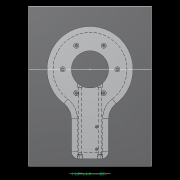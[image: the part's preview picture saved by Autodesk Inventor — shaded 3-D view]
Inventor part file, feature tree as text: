
AUTODESK INVENTOR PART (.ipt)
format: ipt  version: 2022.2 (Build 262287010, 287A)  size: 793,600 bytes
history: native  units: mm
features: extrude x36, sketch x23, other x20, pattern_circular x11, plane x7, fillet x6, draft x3, move_body x2, revolve x2, chamfer x2, projected_geometry x1
ambient origin geometry x8: Origin, YZ Plane, XZ Plane, XY Plane, X Axis, Y Axis, Z Axis, Center Point
bodies: Solid5 (feature_tree)
feature tree (113):
  other  "CrossSection1"
  other  "CrossSection2"
  sketch  "Sketch7"  dims[d167=8.972256mm]
  other  "Roller1"
  other  "Roller2"
  sketch  "Sketch22"  dims[d173=10.814812mm]
  sketch  "Sketch2"  dims[d57=4.025mm d90=61.984365mm]
  sketch  "Sketch23"  dims[d201=75.0mm d232=0.0mm d233=3600.0mm]
  other  "RevRoller1"
  fillet  "Fillet1"  Radius=59.246882mm
  extrude  "Extrusion39"  Depth=61.984365mm
  pattern_circular  "Circular Pattern13"  Count=360  [1 undecoded]
  move_body  "Move Body7"
  revolve  "Revolution13"  [1 undecoded]
  fillet  "Fillet3"  Radius=0.025mm
  pattern_circular  "Circular Pattern14"  Count=24  [1 undecoded]
  move_body  "Move Body6"
  revolve  "Revolution14"  [1 undecoded]
  other  "OuterRim_Top2"
  other  "OuterRim_Bottom2"
  plane  "Work Plane8"
  sketch  "Sketch49"  dims[d352=0.025mm]
  sketch  "Sketch50"  dims[d354=0.025mm]
  sketch  "Sketch51"  dims[d355=16.1595mm]
  extrude  "Extrusion40"  Depth=0.025mm
  extrude  "Extrusion41"  Depth=1.308997mm
  extrude  "Extrusion42"  Depth=0.5mm
  extrude  "Extrusion43"  TaperAngle=360.0deg  [1 undecoded]
  sketch  "Sketch52"  dims[d356=16.159664mm]
  extrude  "Extrusion44"  Depth=7.0mm
  extrude  "Extrusion45"  Depth=7.0mm
  extrude  "Extrusion46"  Depth=7.0mm
  extrude  "Extrusion47"  Depth=7.0mm
  pattern_circular  "Circular Pattern32"  [2 undecoded]
  pattern_circular  "Circular Pattern33"  [2 undecoded]
  sketch  "Sketch57"  dims[d358=360.0deg]
  extrude  "Extrusion50"  TaperAngle=0.0deg  [1 undecoded]
  extrude  "Extrusion51"  TaperAngle=0.0deg  [1 undecoded]
  pattern_circular  "Circular Pattern34"  [2 undecoded]
  extrude  "Extrusion52"  Depth=7.0mm
  extrude  "Extrusion53"  Depth=7.0mm
  pattern_circular  "Circular Pattern35"  [2 undecoded]
  plane  "Work Plane9"
  sketch  "Sketch59"  dims[d361=360.0deg d363=1.308997mm]
  extrude  "Extrusion54"  Depth=7.0mm
  draft  "FaceDraft7"
  extrude  "Extrusion59"  Depth=7.0mm
  extrude  "Extrusion60"  TaperAngle=90.0deg  [1 undecoded]
  fillet  "Fillet5"  [1 undecoded]
  plane  "Work Plane10"
  extrude  "Extrusion63"  TaperAngle=90.0deg  [1 undecoded]
  fillet  "Fillet7"  Radius=75.0mm
  plane  "Work Plane11"
  sketch  "Sketch61"  dims[d371=1.0mm d372=1.308997mm]
  sketch  "Sketch62"  dims[d373=90.0deg d374=0.5mm]
  extrude  "Extrusion64"  Depth=7.0mm
  extrude  "Extrusion65"  TaperAngle=0.0deg  [1 undecoded]
  fillet  "Fillet8"  Radius=0.436332mm
  extrude  "Extrusion66"  Depth=2.0mm TaperAngle=0.0deg
  fillet  "Fillet9"  Radius=2.5mm
  extrude  "Extrusion67"  Depth=8.0mm
  plane  "Work Plane7"
  sketch  "Sketch47"  dims[d350=47.575427mm]
  extrude  "Rotor_Ring"  Depth=8.0mm
  draft  "FaceDraft2"
  sketch  "Sketch30"  dims[d343=16.1595mm d344=16.159664mm d345=0.025mm]
  plane  "Work Plane5"
  other  "Rotor Featurs"
  other  "RotorRim_Bottom"
  extrude  "Extrusion24"  Depth=7.0mm TaperAngle=30.0deg
  extrude  "Extrusion25"  Depth=7.0mm
  extrude  "Extrusion26"  Depth=7.0mm TaperAngle=30.0deg
  pattern_circular  "Circular Pattern23"  [2 undecoded]
  sketch  "Sketch41"  dims[d347=0.1mm]
  extrude  "Extrusion27"  Depth=7.0mm
  extrude  "Extrusion28"  Depth=7.0mm
  pattern_circular  "Circular Pattern24"  Count=10  [1 undecoded]
  extrude  "Extrusion29"  Depth=2.0mm
  extrude  "Extrusion30"  Depth=7.0mm
  extrude  "Extrusion31"  Depth=7.0mm
  pattern_circular  "Circular Pattern25"  [2 undecoded]
  sketch  "Sketch42"  dims[d348=0.1mm]
  extrude  "Extrusion32"  Depth=7.0mm
  extrude  "Extrusion33"  Depth=7.0mm
  extrude  "Extrusion34"  Depth=7.0mm
  extrude  "Extrusion35"  Depth=7.0mm
  pattern_circular  "Circular Pattern26"  [2 undecoded]
  pattern_circular  "Circular Pattern27"  [2 undecoded]
  chamfer  "Chamfer1"  Distance=3.0mm
  chamfer  "Chamfer2"  Distance=2.4mm
  draft  "FaceDraft4"
  plane  "Work Plane6"
  sketch  "Sketch43"  dims[d349=47.575591mm]
  extrude  "Extrusion37"  TaperAngle=0.0deg  [1 undecoded]
  extrude  "Extrusion38"  TaperAngle=0.0deg  [1 undecoded]
  other  "2D Equation Curve1"
  sketch  "Sketch40"  dims[d346=0.025mm]
  other  "Work Axis6"
  other  "Work Axis7"
  other  "Work Axis8"
  other  "Work Axis9"
  other  "Work Axis10"
  other  "Work Point1"
  other  "Work Point2"
  other  "Work Point3"
  other  "Work Point4"
  other  "Work Point5"
  sketch  "Sketch48"  dims[d351=0.025mm]
  sketch  "Sketch58"  dims[d359=0.5mm d360=240.0mm]
  sketch  "Sketch60"  dims[d367=8.1mm d370=0.025mm]
  projected_geometry  "Projected Loop1"
  sketch  "Sketch63"  dims[d375=240.0mm d376=360.0deg]
  sketch  "Sketch64"  dims[d378=90.0deg d379=0.1mm d380=0.025mm d381=0.025mm d382=0.025mm d383=0.025mm d384=11.193516mm d385=0.0mm d386=0.0mm d391=25.0mm d392=75.0mm d393=1.5mm d394=1.5mm d395=1.5mm d396=1.5mm d397=90.0deg d398=90.0deg d399=90.0deg d400=75.0mm d401=11.193516mm d402=0.0mm d486=0.436332mm d487=0.5mm d488=2.0mm d489=0.0mm d490=20.0mm d495=2.5mm d496=8.0mm d506=13.856406mm d507=55.5mm d508=8.0mm d509=0.05mm d510=2.5mm d511=30.0deg d512=12.0mm d513=6.0mm d514=0.2mm d515=30.0deg d516=131.0mm d517=65.5mm d518=0.2mm d519=100.0mm d520=120.0mm d521=2.0mm d522=150.0mm d530=50.0mm d531=5.5mm d532=5.5mm d533=5.5mm d534=85.75mm d535=73.5mm d536=61.25mm d537=24.5mm d538=3.0mm d539=2.4mm d540=0.0mm d541=0.0mm d542=0.0mm d543=5.5mm d544=3.0mm d545=0.0mm d546=90.0mm d547=360.0deg d549=3.0mm d550=3.0mm d551=2.4mm d552=0.0mm d553=5.596758mm d554=0.0mm d555=2.4mm d556=0.0mm d557=5.596758mm d558=0.0mm d559=5.596758mm d560=0.0mm d561=90.0mm d562=360.0deg d564=60.0mm d565=360.0deg d567=5.5mm d568=5.5mm d569=3.0mm d570=0.0mm d571=5.596758mm d572=0.0mm d573=3.0mm d574=0.0mm d575=5.596758mm d576=0.0mm d577=90.0mm d578=360.0deg d580=60.0mm d581=360.0deg d584=20.0mm d585=8.0mm d587=1.75mm d589=3.0mm d592=2.0mm d593=12.0mm d594=12.0mm d600=0.5mm d601=2.0mm d602=45.0deg d603=0.5mm d604=2.0mm d605=45.0deg d606=0.436332mm d607=0.5mm d608=0.0mm d609=20.0mm d611=360.0deg d613=0.0mm d614=0.0mm d617=0.99971mm d618=100.0mm d620=69.0mm d621=5.0mm d622=0.5mm d623=0.5mm d624=5.0mm d625=0.2mm d626=0.0mm d627=20.0mm d629=69.0mm d630=73.5mm d631=20.0mm d633=6.283185mm d635=5.5mm d636=3.0mm d637=7.0mm d638=4.0mm d639=5.596758mm d640=0.0mm d641=3.0mm d642=0.0mm d643=5.596758mm d644=0.0mm d645=4.0mm d646=0.0mm d647=20.0mm d649=6.283185mm d651=3.0mm d652=4.0mm d653=20.0mm d655=6.283185mm d657=7.0mm d658=5.5mm d659=5.596758mm d660=0.0mm d661=2.593516mm d662=0.0mm d663=5.596758mm d664=0.0mm d665=3.193516mm d666=0.0mm d679=50.0mm d680=360.0deg d682=50.0mm d683=360.0deg d694=6.35mm d695=6.35mm d696=6.9mm d697=5.9mm d698=11.194mm d699=0.0mm d700=8.194mm d701=0.0mm d702=60.0mm d703=360.0deg d705=30.0deg d706=4.0mm d707=7.0mm d708=3.193516mm d709=0.0mm d710=11.193516mm d711=0.0mm d712=60.0mm d713=360.0deg d715=20.0mm d716=77.0mm d717=9.0mm d718=30.0mm d719=4.0mm d720=4.0mm d721=120.0mm d722=90.0deg d723=1.0mm d724=0.0mm d734=0.436332mm d737=1.0mm d738=0.0mm d739=1.0mm d740=0.0mm d741=25.0mm d742=0.5mm d743=2.0mm d744=0.0mm d745=20.0mm d746=50.0mm d747=77.0mm d748=9.0mm d749=30.0mm d750=4.0mm d751=4.0mm d752=120.0mm d759=8.0mm d760=0.0mm d761=25.0mm d762=20.0mm d763=4.1mm d764=14.0mm d765=4.1mm d766=8.0mm d767=0.0mm d769=4.5mm d770=11.5mm d771=7.0mm d772=7.0mm d773=23.712mm d774=0.0mm d775=10.0mm d776=60.0mm d778=360.0deg d780=7.0mm d781=4.0mm d782=0.0mm d783=8.0mm d784=7.0mm d785=7.0mm d786=26.0mm d787=0.0mm d16=0.872665mm d17=0.872665mm d49=0.872665mm d50=0.872665mm d51=0.872665mm d52=0.872665mm d236=0.5mm d237=0.872665mm d238=0.5mm d239=0.872665mm d282=1.0mm d283=1.0mm d284=1.0mm d285=0.15mm d286=0.25mm d287=0.375mm d288=14.3117mm d289=0.75mm d290=20.594885mm d291=0.0625mm d292=0.75mm d293=0.375mm d405=0.5mm d406=0.872665mm d407=0.5mm d408=0.872665mm d413=0.5mm d414=0.872665mm d415=0.5mm d416=0.872665mm d417=0.5mm d418=0.872665mm d419=0.5mm d420=0.872665mm d421=0.872665mm d431=0.5mm d432=0.872665mm d433=0.5mm d434=0.872665mm d471=0.5mm d472=0.872665mm d473=0.5mm d474=0.872665mm d497=0.5mm d498=0.872665mm d499=0.5mm d500=0.872665mm d590=0.5mm d591=0.872665mm d729=0.5mm d730=0.872665mm d731=0.5mm d732=0.872665mm]
note: 30 required parameter values undecoded (feature->parameter linkage not recoverable at this tier; creation-order binding heuristic only, values carry confidence <= 0.55)